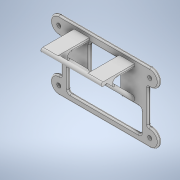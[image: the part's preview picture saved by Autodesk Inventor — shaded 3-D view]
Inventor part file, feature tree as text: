
AUTODESK INVENTOR PART (.ipt)
format: ipt  version: 2020.3 (Build 243373000, 373)  size: 505,344 bytes
history: native  units: mm
features: extrude x8, fillet x8, sketch x8, pattern_linear x1
ambient origin geometry x8: Origin, YZ Plane, XZ Plane, XY Plane, X Axis, Y Axis, Z Axis, Center Point
bodies: Solid1 (feature_tree)
feature tree (25):
  extrude  "Extrusion1"  Depth=38.8mm
  extrude  "Extrusion2"  Depth=3.0mm
  extrude  "Extrusion3"  Depth=3.0mm
  extrude  "Extrusion4"  Depth=2.5mm TaperAngle=0.0deg
  fillet  "Fillet1"  Radius=45.0mm
  extrude  "Extrusion5"  Depth=3.0mm
  fillet  "Fillet2"  Radius=25.0mm
  pattern_linear  "Rectangular Pattern1"  Spacing1=3.0mm  [1 undecoded]
  extrude  "Extrusion6"  Depth=1.0mm TaperAngle=0.0deg
  fillet  "Fillet3"  Radius=22.5mm
  fillet  "Fillet4"  Radius=30.0mm
  fillet  "Fillet5"  Radius=2.0mm
  extrude  "Extrusion7"  Depth=1.0mm
  fillet  "Fillet7"  Radius=7.0mm
  fillet  "Fillet8"  Radius=3.0mm
  extrude  "Extrusion8"  Depth=1.0mm TaperAngle=0.0deg
  fillet  "Fillet10"  Radius=20.0mm
  sketch  "Sketch1"  dims[d0=68.0mm d1=38.8mm]
  sketch  "Sketch2"  dims[d2=3.0mm d3=3.0mm]
  sketch  "Sketch3"  dims[d4=3.0mm d5=3.0mm]
  sketch  "Sketch4"  dims[d6=6.5mm d7=2.5mm d8=0.0mm d9=45.0mm]
  sketch  "Sketch7"  dims[d10=3.0mm d11=3.0mm d12=25.0mm d13=0.0mm]
  sketch  "Sketch8"  dims[d14=3.0mm]
  sketch  "Sketch9"  dims[d15=3.0mm]
  sketch  "Sketch10"  dims[d16=45.0deg d17=3.0mm d18=30.0mm d19=0.0mm d20=22.5mm d21=30.0mm d22=0.0mm d23=2.0mm d24=1.5mm d25=7.0mm d26=3.0mm d27=1.0mm d28=0.0mm d29=20.0mm d31=68.0mm d32=20.0mm d34=38.8mm d35=6.5mm d36=1.0mm d37=1.5mm d38=0.0mm d39=0.0mm d40=45.0mm d41=1.5mm d42=1.5mm d43=1.5mm d45=5.0mm d46=5.0mm d47=5.0mm d48=1.0mm d49=1.0mm d50=0.0mm d51=2.0mm d52=1.0mm d55=10.0mm d56=0.0mm d59=1.0mm d60=5.0mm]
note: 1 required parameter value undecoded (feature->parameter linkage not recoverable at this tier; creation-order binding heuristic only, values carry confidence <= 0.55)
